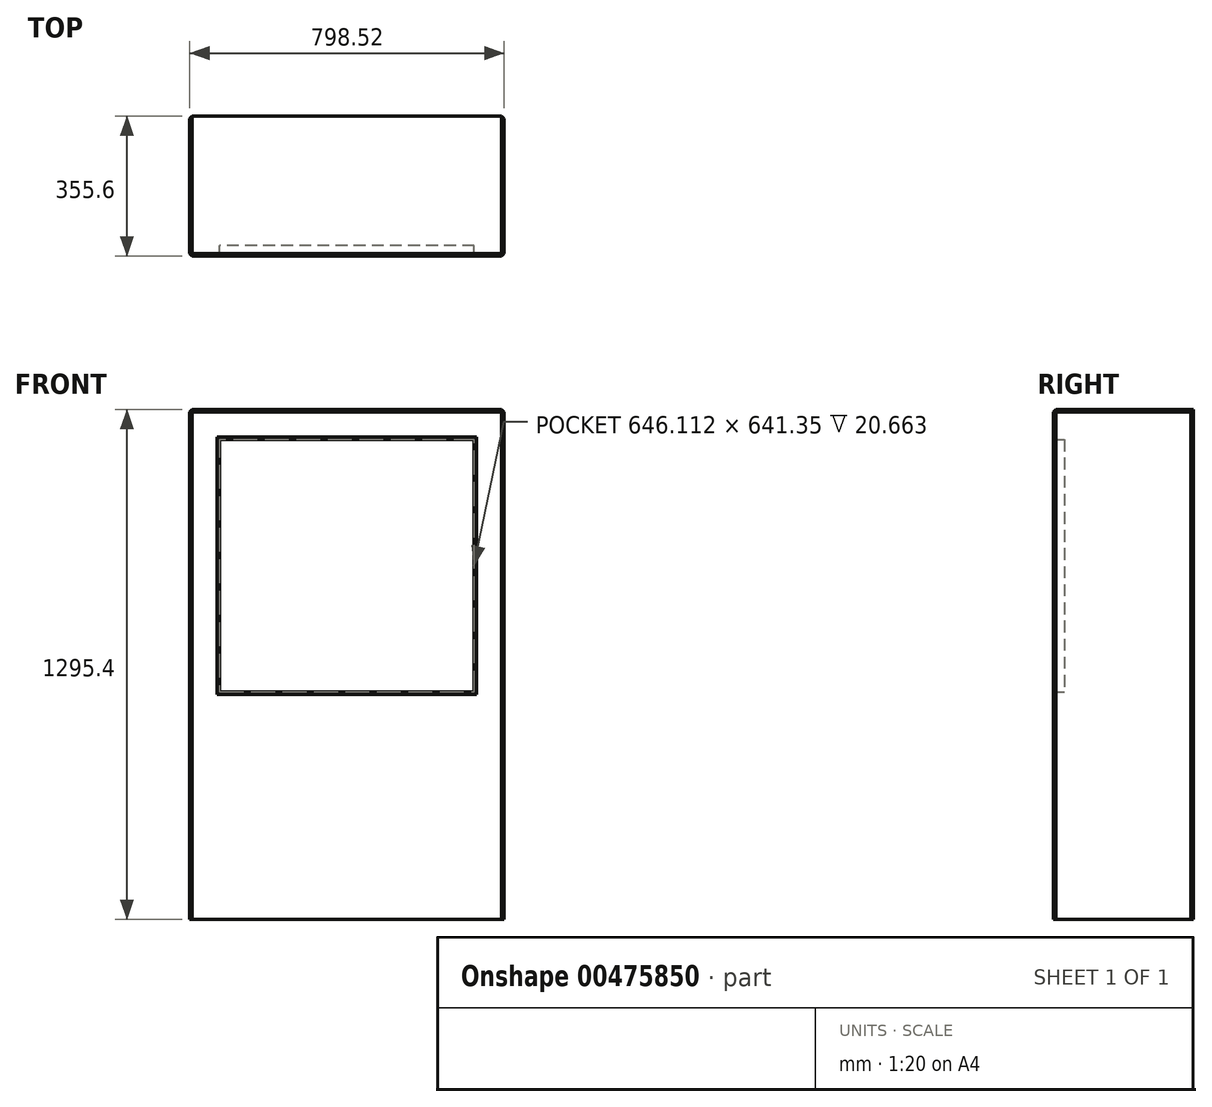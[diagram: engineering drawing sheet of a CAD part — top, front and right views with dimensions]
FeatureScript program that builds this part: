
annotation { "Feature Type Name" : "Feature", "Feature Type Description" : "" }
export const myFeature = defineFeature(function(context is Context, id is Id, definition is map)
    precondition{}
    {
        {
            var Q0;
            Q0=qCreatedBy(makeId("Front.planeOp"),FACE);
            var sketch = newSketch(context, id + "F0", { "sketchPlane" : qUnion([Q0])});
            skLineSegment(sketch, "E0.bottom", {"start": v(399.26, -647.7) * mm, "end": v(-399.26, -647.7) * mm});
            skLineSegment(sketch, "E0.top", {"start": v(399.26, 647.7) * mm, "end": v(-399.26, 647.7) * mm});
            skLineSegment(sketch, "E0.left", {"start": v(399.26, -647.7) * mm, "end": v(399.26, 647.7) * mm});
            skLineSegment(sketch, "E0.right", {"start": v(-399.26, -647.7) * mm, "end": v(-399.26, 647.7) * mm});
            skPoint(sketch, "E0.middle", {"position": v(0, 0) * mm});
            skLineSegment(sketch, "E1", {"start": v(323.06, 323.85) * mm, "end": v(323.06, -69.85) * mm});
            skLineSegment(sketch, "E2.bottom", {"start": v(323.06, -69.85) * mm, "end": v(-323.06, -69.85) * mm});
            skLineSegment(sketch, "E2.top", {"start": v(323.06, 571.5) * mm, "end": v(-323.06, 571.5) * mm});
            skLineSegment(sketch, "E2.left", {"start": v(323.06, -69.85) * mm, "end": v(323.06, 571.5) * mm});
            skLineSegment(sketch, "E2.right", {"start": v(-323.06, -69.85) * mm, "end": v(-323.06, 571.5) * mm});
            skSolve(sketch);
        }
        {
            var Q0;
            Q0=makeQuery(id+"F0.imprint","IMPRINT",FACE,{"disambiguationData":[TD([[makeQuery(id+"F0.imprint","IMPRINT",EDGE,{"derivedFrom":sQuery(id+"F0.wireOp",EDGE,"E0.bottom")}),-1.0]])]});
            extrude(context, id + "F1", {"entities" : qUnion([Q0]), "depth" : 355.6 * mm});
        }
        {
            var Q0;
            {var subQ3=sQuery(id+"F0.wireOp",EDGE,"E2.bottom");Q0=makeQuery(id+"F0.imprint","IMPRINT",FACE,{"disambiguationData":[TD([[makeQuery(id+"F0.imprint","IMPRINT",EDGE,{"derivedFrom":subQ3}),-1.0]])]});}
            extrude(context, id + "F2", {"entities" : qUnion([Q0]), "operationType" : NewBodyOperationType.ADD, "depth" : 328.59 * mm});
        }
        {
            var Q0;
            Q0=makeQuery(id+"F1.opExtrude","CAP_EDGE",EDGE,{"disambiguationData":[OSD([sQuery(id+"F0.wireOp",EDGE,"E2.bottom")])],"isStart":false});
            var Q1;
            Q1=makeQuery(id+"F1.opExtrude","CAP_EDGE",EDGE,{"disambiguationData":[OSD([sQuery(id+"F0.wireOp",EDGE,"E2.right")])],"isStart":false});
            var Q2;
            Q2=makeQuery(id+"F1.opExtrude","CAP_EDGE",EDGE,{"disambiguationData":[OSD([sQuery(id+"F0.wireOp",EDGE,"E2.top")])],"isStart":false});
            var Q3;
            Q3=makeQuery(id+"F1.opExtrude","CAP_EDGE",EDGE,{"disambiguationData":[OSD([sQuery(id+"F0.wireOp",EDGE,"E2.left")])],"isStart":false});
            chamfer(context, id + "F3", {"entities" : qUnion([Q0, Q1, Q2, Q3]), "width" : 6.35 * mm, "tangentPropagation" : true});
        }
        {
            var Q0;
            Q0=makeQuery(id+"F1.opExtrude","CAP_EDGE",EDGE,{"disambiguationData":[OSD([sQuery(id+"F0.wireOp",EDGE,"E0.left")])],"isStart":false});
            var Q1;
            Q1=makeQuery(id+"F1.opExtrude","CAP_EDGE",EDGE,{"disambiguationData":[OSD([sQuery(id+"F0.wireOp",EDGE,"E0.top")])],"isStart":false});
            var Q2;
            Q2=makeQuery(id+"F1.opExtrude","CAP_EDGE",EDGE,{"disambiguationData":[OSD([sQuery(id+"F0.wireOp",EDGE,"E0.right")])],"isStart":false});
            var Q3;
            Q3=makeQuery(id+"F1.opExtrude","SWEPT_EDGE",EDGE,{"disambiguationData":[OSD([sQuery(id+"F0.wireOp",EDGE,"E0.top"),sQuery(id+"F0.wireOp",EDGE,"E0.right")])]});
            var Q4;
            Q4=makeQuery(id+"F1.opExtrude","SWEPT_EDGE",EDGE,{"disambiguationData":[OSD([sQuery(id+"F0.wireOp",EDGE,"E0.top"),sQuery(id+"F0.wireOp",EDGE,"E0.left")])]});
            var Q5;
            Q5=makeQuery(id+"F1.opExtrude","CAP_EDGE",EDGE,{"disambiguationData":[OSD([sQuery(id+"F0.wireOp",EDGE,"E0.right")])],"isStart":true});
            var Q6;
            Q6=makeQuery(id+"F1.opExtrude","CAP_EDGE",EDGE,{"disambiguationData":[OSD([sQuery(id+"F0.wireOp",EDGE,"E0.left")])],"isStart":true});
            chamfer(context, id + "F4", {"entities" : qUnion([Q0, Q1, Q2, Q3, Q4, Q5, Q6]), "width" : 6.35 * mm, "tangentPropagation" : true});
        }
    });
